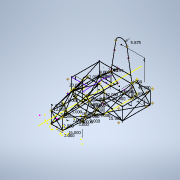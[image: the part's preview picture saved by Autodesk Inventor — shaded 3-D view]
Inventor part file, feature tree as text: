
AUTODESK INVENTOR PART (.ipt)
format: ipt  version: 2021 (Build 250183000, 183)  size: 265,728 bytes
history: native  units: in
note: dims shown in document units (in); Inventor stores cm internally (conversion verified against a paired STEP export)
features: other x46, plane x38, sketch x27
ambient origin geometry x8: Origin, YZ Plane, XZ Plane, XY Plane, X Axis, Y Axis, Z Axis, Center Point
feature tree (111):
  sketch  "Sketch1"  dims[d0=12.0in]
  plane  "Work Plane1"
  sketch  "Sketch2"  dims[d1=12.0in]
  plane  "Work Plane2"
  plane  "Work Plane3"
  sketch  "Sketch3"  dims[d2=2.0in]
  plane  "Work Plane4"
  plane  "Work Plane5"
  plane  "Work Plane6"
  plane  "Work Plane7"
  plane  "Work Plane8"
  plane  "Work Plane9"
  other  "Work Point1"
  other  "Work Point2"
  other  "Work Point3"
  other  "Work Point4"
  other  "Work Point5"
  other  "Work Point6"
  other  "Work Point7"
  other  "Work Point8"
  other  "Work Point9"
  other  "Work Point10"
  other  "Work Point11"
  other  "Work Point12"
  other  "Work Point13"
  other  "Work Point14"
  other  "Work Point15"
  other  "Work Point16"
  other  "Work Point17"
  other  "Work Point18"
  other  "Work Point19"
  other  "Work Point20"
  other  "Work Point21"
  other  "Work Point22"
  other  "Work Point23"
  other  "Work Point24"
  other  "Work Point27"
  other  "Work Point28"
  other  "Work Point29"
  other  "Work Point30"
  other  "Work Point31"
  other  "Work Point32"
  other  "Work Point33"
  other  "Work Point34"
  other  "Work Point35"
  other  "Work Point36"
  other  "Work Point38"
  other  "Work Point40"
  other  "Work Point41"
  other  "Work Point42"
  other  "Work Point43"
  other  "Work Point44"
  plane  "Work Plane10"
  sketch  "Sketch11"  dims[d3=-18.5in]
  plane  "Work Plane11"
  sketch  "Sketch12"  dims[d4=16.0in]
  plane  "Work Plane12"
  sketch  "Sketch13"  dims[d5=2.0in]
  plane  "Work Plane13"
  sketch  "Sketch14"  dims[d6=3.0in]
  plane  "Work Plane14"
  sketch  "Sketch15"  dims[d7=6.0in]
  plane  "Work Plane15"
  sketch  "Sketch16"  dims[d8=3.0in]
  plane  "Work Plane16"
  sketch  "Sketch17"  dims[d9=6.0in]
  plane  "Work Plane17"
  sketch  "Sketch18"  dims[d10=-6.0in d11=-6.0in]
  other  "Work Point55"
  other  "Work Point56"
  other  "Work Point57"
  other  "Work Point58"
  plane  "Work Plane18"
  sketch  "Sketch19"  dims[d12=16.0in]
  plane  "Work Plane19"
  sketch  "Sketch20"  dims[d13=2.0in]
  plane  "Work Plane20"
  sketch  "Sketch21"  dims[d14=3.0in]
  plane  "Work Plane21"
  sketch  "Sketch22"  dims[d15=3.0in]
  plane  "Work Plane22"
  sketch  "Sketch23"  dims[d16=6.0in]
  plane  "Work Plane23"
  sketch  "Sketch24"  dims[d17=6.0in]
  plane  "Work Plane24"
  sketch  "Sketch25"  dims[d18=-7.5in]
  plane  "Work Plane25"
  sketch  "Sketch26"  dims[d19=22.0in]
  plane  "Work Plane26"
  sketch  "Sketch27"  dims[d21=20.0in]
  plane  "Work Plane27"
  sketch  "Sketch28"  dims[d23=12.0in]
  plane  "Work Plane28"
  sketch  "Sketch29"  dims[d24=25.0in]
  plane  "Work Plane29"
  plane  "Work Plane36"
  plane  "Work Plane37"
  plane  "Work Plane39"
  plane  "Work Plane53"
  sketch  "Sketch41"  dims[d26=13.0in]
  plane  "Work Plane41"
  sketch  "Sketch42"  dims[d31=-29.4in]
  plane  "Work Plane43"
  sketch  "Sketch44"  dims[d32=22.0in]
  plane  "Work Plane44"
  other  "Work Point63"
  other  "Work Point64"
  plane  "Work Plane50"
  sketch  "Sketch51"  dims[d33=13.0in d34=13.0in d42=5.875in d45=-6.0in d52=-7.5in d58=-6.0in d61=-6.0in d67=9.8in d68=9.8in d69=22.0in d85=7.0in d105=4.299in d109=0.0831in d110=8.0in d113=8.0in d114=4.299in d116=0.0831in d118=0.5in d122=3.5483in d124=15.5in d125=4.0in d126=43.5in d127=2.0in d128=2.0in d129=2.0in d130=2.0in]
  plane  "Work Plane56"
  sketch  "3D Sketch1"
